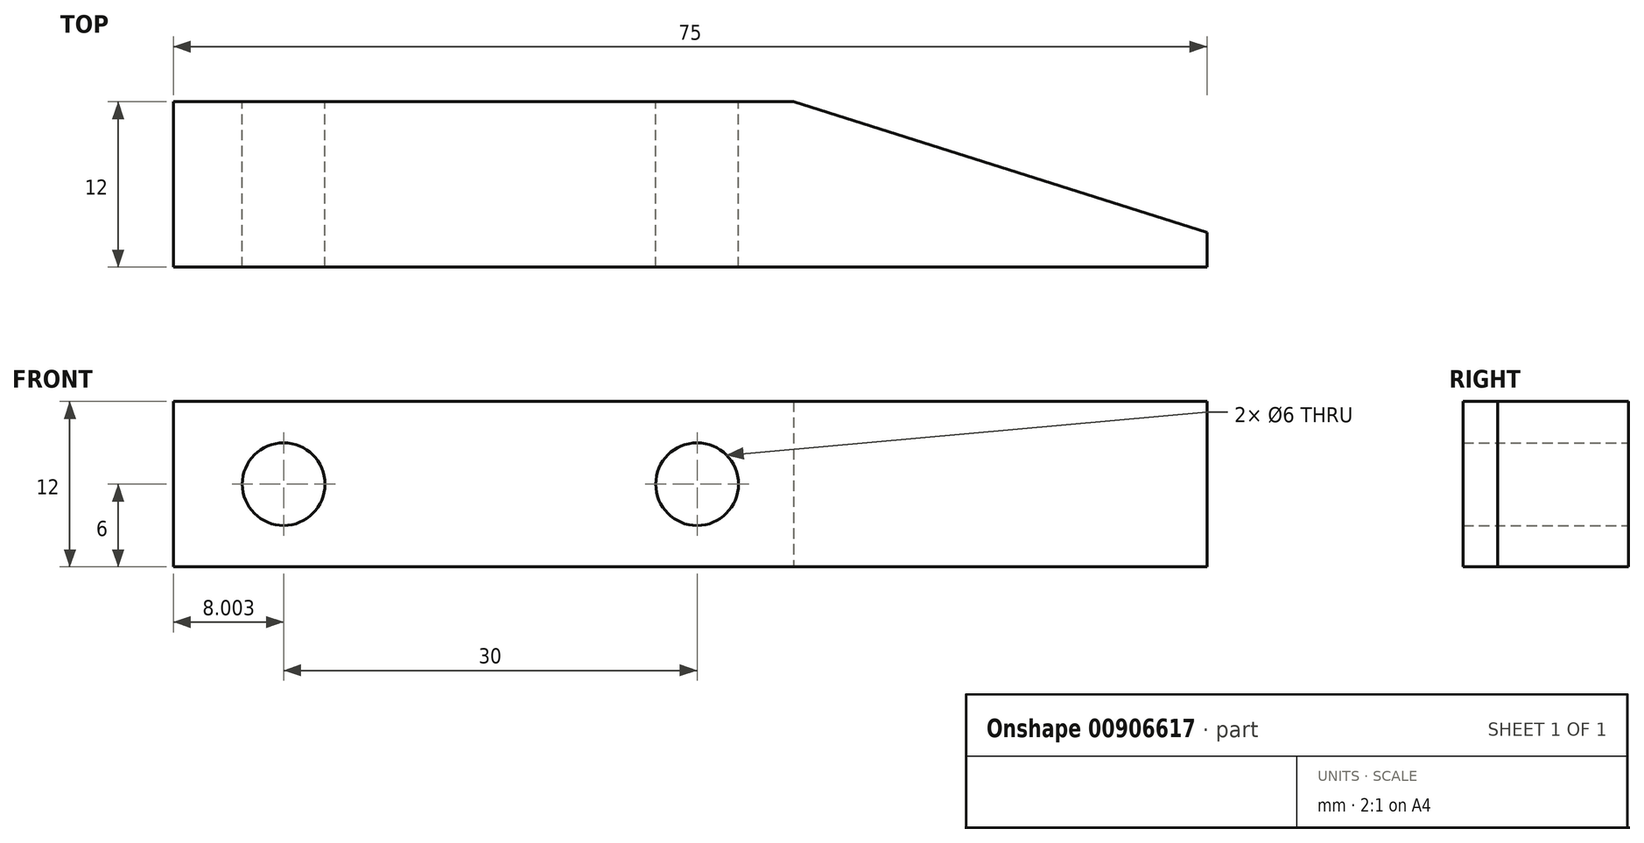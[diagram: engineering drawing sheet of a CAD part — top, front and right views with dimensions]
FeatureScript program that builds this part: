
annotation { "Feature Type Name" : "Feature", "Feature Type Description" : "" }
export const myFeature = defineFeature(function(context is Context, id is Id, definition is map)
    precondition{}
    {
        {
            var Q0;
            Q0=qCreatedBy(makeId("Top.planeOp"),FACE);
            var sketch = newSketch(context, id + "F0", { "sketchPlane" : qUnion([Q0])});
            skLineSegment(sketch, "E0", {"start": v(-19.32, 22.42) * mm, "end": v(25.68, 22.42) * mm});
            skLineSegment(sketch, "E1", {"start": v(25.68, 22.42) * mm, "end": v(55.68, 12.92) * mm});
            skLineSegment(sketch, "E2", {"start": v(55.68, 12.92) * mm, "end": v(55.68, 10.42) * mm});
            skLineSegment(sketch, "E3", {"start": v(55.68, 10.42) * mm, "end": v(-19.32, 10.42) * mm});
            skLineSegment(sketch, "E4", {"start": v(-19.32, 10.42) * mm, "end": v(-19.32, 22.42) * mm});
            skSolve(sketch);
        }
        {
            var Q0;
            Q0=makeQuery(id+"F0.imprint","IMPRINT",FACE,{"disambiguationData":[TD([[makeQuery(id+"F0.imprint","IMPRINT",EDGE,{"derivedFrom":sQuery(id+"F0.wireOp",EDGE,"E0")}),-1.0]])]});
            extrude(context, id + "F1", {"entities" : qUnion([Q0]), "depth" : 12 * mm, "offsetDistance" : 25 * mm});
        }
        {
            var Q0;
            Q0=makeQuery(id+"F1.opExtrude","SWEPT_FACE",FACE,{"disambiguationData":[OSD([sQuery(id+"F0.wireOp",EDGE,"E0")])]});
            var sketch = newSketch(context, id + "F2", { "sketchPlane" : qUnion([Q0])});
            skPoint(sketch, "E5", {"position": v(-18.68, 6) * mm});
            skPoint(sketch, "E6", {"position": v(11.32, 6) * mm});
            skCircle(sketch, "E7", {"center": v(-18.68, 6) * mm, "radius": 3 * mm});
            skCircle(sketch, "E8", {"center": v(11.32, 6) * mm, "radius": 3 * mm});
            skSolve(sketch);
        }
        {
            var Q0;
            Q0 = qSketchRegion(id + "F2", true);
            extrude(context, id + "F3", {"entities" : qUnion([Q0]), "operationType" : NewBodyOperationType.REMOVE, "endBound" : BoundingType.THROUGH_ALL, "oppositeDirection" : true, "depth" : 25 * mm, "offsetDistance" : 25 * mm});
        }
    });
